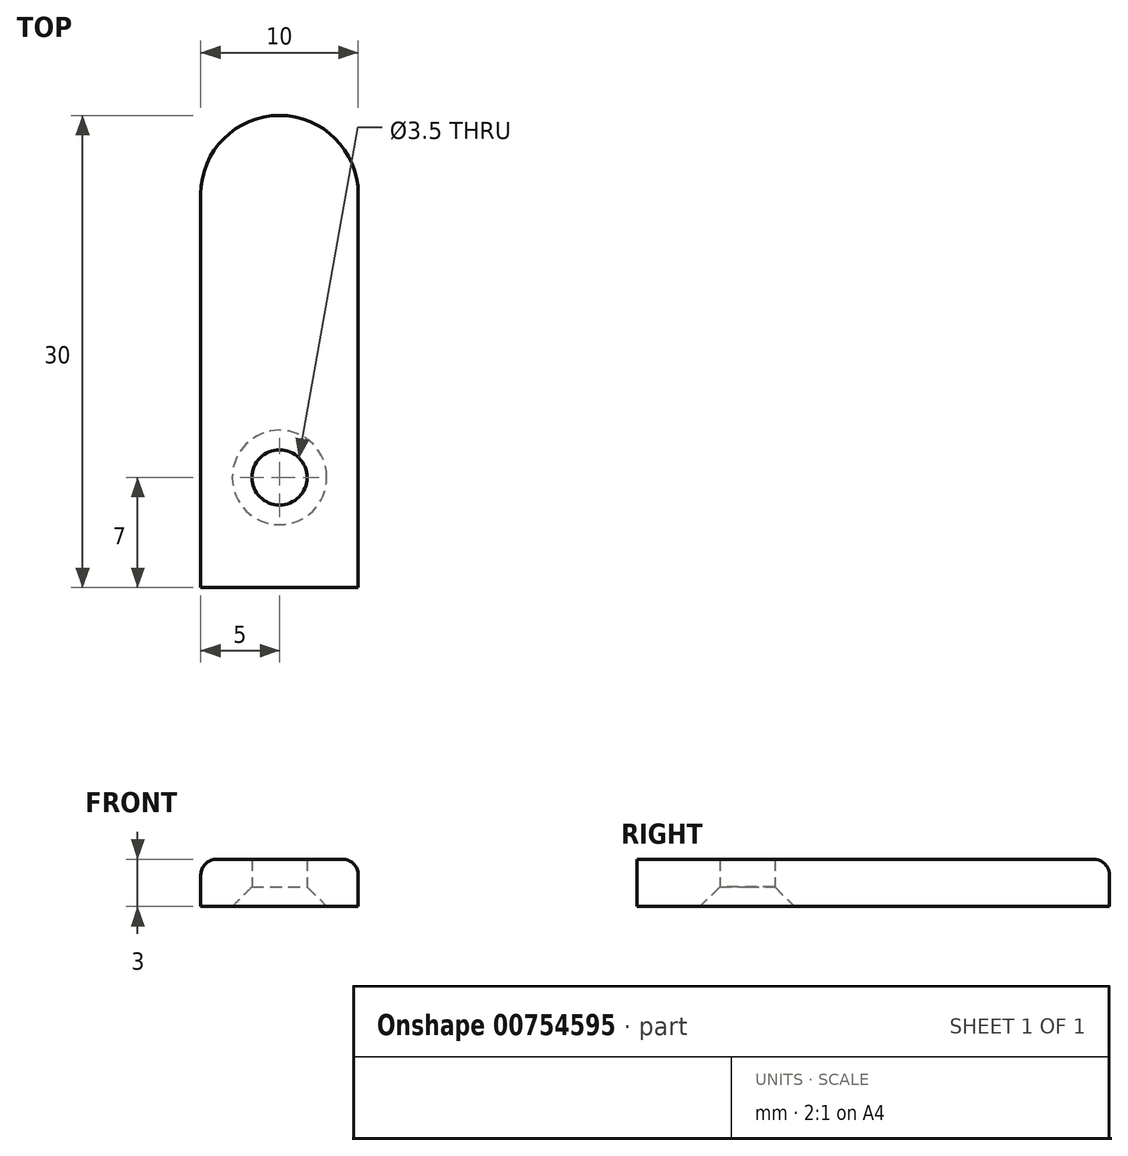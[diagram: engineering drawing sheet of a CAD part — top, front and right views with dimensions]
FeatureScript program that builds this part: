
annotation { "Feature Type Name" : "Feature", "Feature Type Description" : "" }
export const myFeature = defineFeature(function(context is Context, id is Id, definition is map)
    precondition{}
    {
        {
            var Q0;
            Q0=qCreatedBy(makeId("Top.planeOp"),FACE);
            var sketch = newSketch(context, id + "F0", { "sketchPlane" : qUnion([Q0])});
            skLineSegment(sketch, "E0.bottom", {"start": v(-5, 0) * mm, "end": v(5, 0) * mm});
            skLineSegment(sketch, "E0.top", {"start": v(-5, 30) * mm, "end": v(5, 30) * mm});
            skLineSegment(sketch, "E0.left", {"start": v(-5, 0) * mm, "end": v(-5, 30) * mm});
            skLineSegment(sketch, "E0.right", {"start": v(5, 0) * mm, "end": v(5, 30) * mm});
            skPoint(sketch, "E1", {"position": v(0, 7) * mm});
            skSolve(sketch);
        }
        {
            var Q0;
            Q0=makeQuery(id+"F0.imprint","IMPRINT",FACE,{"disambiguationData":[TD([[makeQuery(id+"F0.imprint","IMPRINT",EDGE,{"derivedFrom":sQuery(id+"F0.wireOp",EDGE,"E0.bottom")}),1.0]])]});
            extrude(context, id + "F1", {"entities" : qUnion([Q0]), "depth" : 3 * mm, "offsetDistance" : 25 * mm});
        }
        {
            var Q0;
            Q0=sQuery(id+"F0.wireOp",VERTEX,"E1");
            var Q1;
            Q1=makeQuery(id+"F1.opExtrude","SWEPT_BODY",BODY,{"disambiguationData":[OSD([sQuery(id+"F0.wireOp",EDGE,"E0.bottom"),sQuery(id+"F0.wireOp",EDGE,"E0.top"),sQuery(id+"F0.wireOp",EDGE,"E0.left"),sQuery(id+"F0.wireOp",EDGE,"E0.right")])]});
            hole(context, id + "F2", {"style" : HoleStyle.C_SINK, "endStyle" : HoleEndStyle.BLIND, "oppositeDirection" : true, "holeDiameter" : 3.5 * mm, "cSinkDiameter" : 6 * mm, "cSinkAngle" : 90 * degree, "majorDiameter" : 5 * mm, "holeDepth" : 3 * mm, "isTappedThrough" : true, "tappedDepth" : 12 * mm, "tapClearance" : 3, "locations" : qUnion([Q0]), "scope" : qUnion([Q1])});
        }
        {
            var Q0;
            Q0=makeQuery(id+"F1.opExtrude","SWEPT_EDGE",EDGE,{"disambiguationData":[OSD([sQuery(id+"F0.wireOp",EDGE,"E0.top"),sQuery(id+"F0.wireOp",EDGE,"E0.right")])]});
            var Q1;
            Q1=makeQuery(id+"F1.opExtrude","SWEPT_EDGE",EDGE,{"disambiguationData":[OSD([sQuery(id+"F0.wireOp",EDGE,"E0.top"),sQuery(id+"F0.wireOp",EDGE,"E0.left")])]});
            fillet(context, id + "F3", {"entities" : qUnion([Q0, Q1]), "radius" : 5 * mm, "tangentPropagation" : true, "allowEdgeOverflow" : false});
        }
        {
            var Q0;
            {var subQ0=sQuery(id+"F0.wireOp",EDGE,"E0.right");var subQ1=sQuery(id+"F0.wireOp",EDGE,"E0.top");Q0=makeQuery(id+"F3.opFillet","BLEND_EDGE",EDGE,{"blendedFrom":[makeQuery(id+"F1.opExtrude","SWEPT_EDGE",EDGE,{"disambiguationData":[OSD([subQ1,subQ0])]}),makeQuery(id+"F1.opExtrude","CAP_FACE",FACE,{"disambiguationData":[OSD([sQuery(id+"F0.wireOp",EDGE,"E0.bottom"),subQ1,sQuery(id+"F0.wireOp",EDGE,"E0.left"),subQ0])],"isStart":true})],"blendedInto":[makeQuery(id+"F1.opExtrude","CAP_FACE",FACE,{"disambiguationData":[OSD([sQuery(id+"F0.wireOp",EDGE,"E0.bottom"),subQ1,sQuery(id+"F0.wireOp",EDGE,"E0.left"),subQ0])],"isStart":true})]});}
            var Q1;
            {var subQ0=sQuery(id+"F0.wireOp",EDGE,"E0.right");var subQ1=sQuery(id+"F0.wireOp",EDGE,"E0.top");Q1=makeQuery(id+"F3.opFillet","BLEND_EDGE",EDGE,{"blendedFrom":[makeQuery(id+"F1.opExtrude","SWEPT_EDGE",EDGE,{"disambiguationData":[OSD([subQ1,subQ0])]}),makeQuery(id+"F1.opExtrude","CAP_FACE",FACE,{"disambiguationData":[OSD([sQuery(id+"F0.wireOp",EDGE,"E0.bottom"),subQ1,sQuery(id+"F0.wireOp",EDGE,"E0.left"),subQ0])],"isStart":false})],"blendedInto":[makeQuery(id+"F1.opExtrude","CAP_FACE",FACE,{"disambiguationData":[OSD([sQuery(id+"F0.wireOp",EDGE,"E0.bottom"),subQ1,sQuery(id+"F0.wireOp",EDGE,"E0.left"),subQ0])],"isStart":false})]});}
            var Q2;
            Q2=makeQuery(id+"F1.opExtrude","CAP_EDGE",EDGE,{"disambiguationData":[OSD([sQuery(id+"F0.wireOp",EDGE,"E0.left")])],"isStart":false});
            var Q3;
            Q3=makeQuery(id+"F1.opExtrude","CAP_EDGE",EDGE,{"disambiguationData":[OSD([sQuery(id+"F0.wireOp",EDGE,"E0.right")])],"isStart":false});
            fillet(context, id + "F4", {"entities" : qUnion([Q0, Q1, Q2, Q3]), "radius" : 1 * mm, "tangentPropagation" : true, "allowEdgeOverflow" : false});
        }
    });
